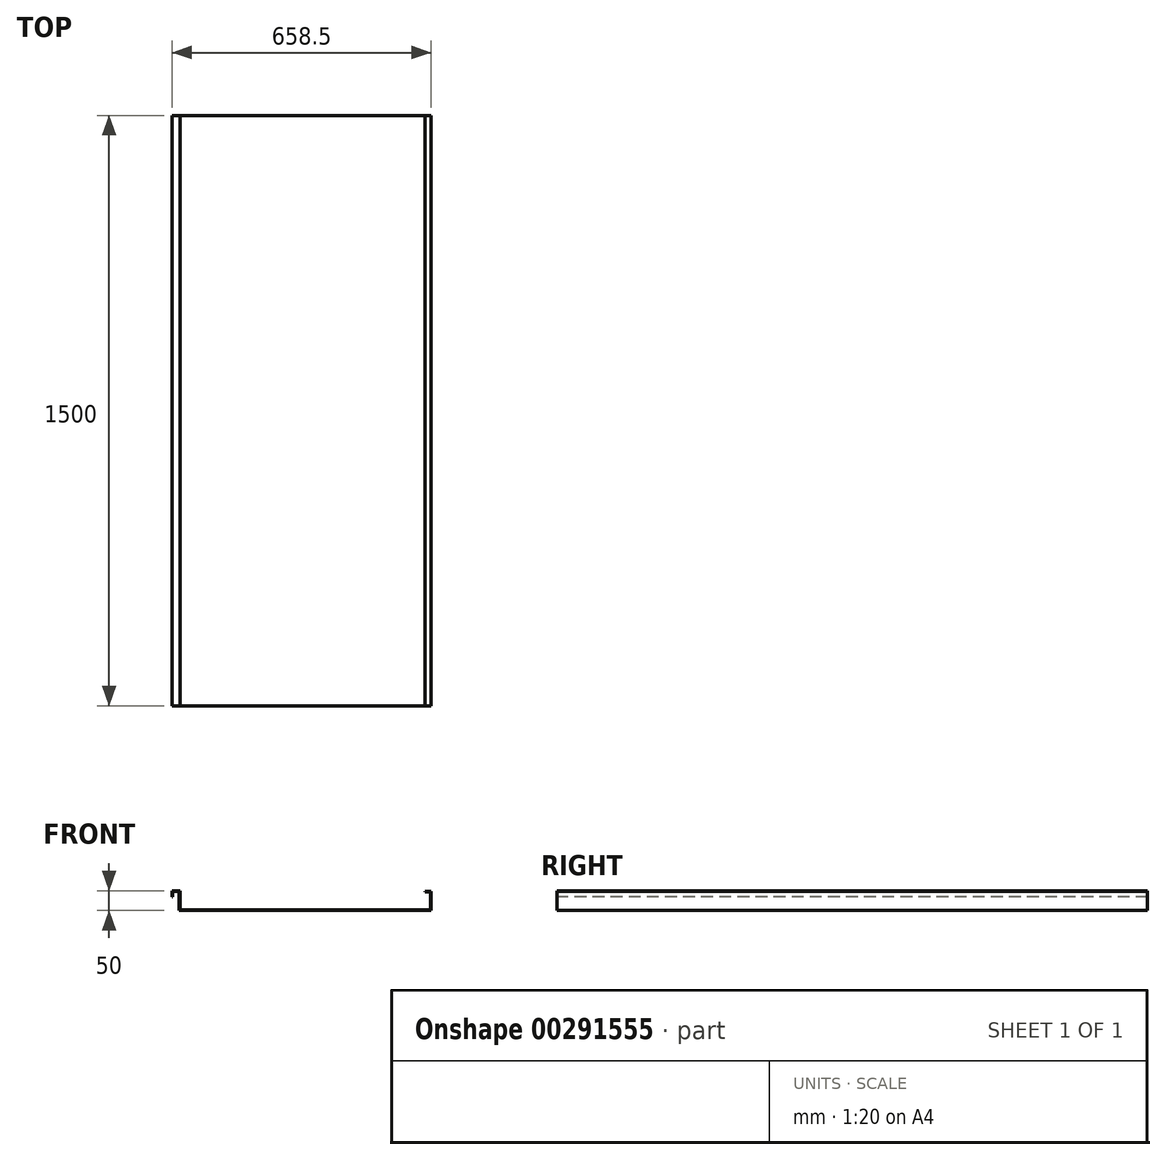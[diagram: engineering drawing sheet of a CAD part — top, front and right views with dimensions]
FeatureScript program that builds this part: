
annotation { "Feature Type Name" : "Feature", "Feature Type Description" : "" }
export const myFeature = defineFeature(function(context is Context, id is Id, definition is map)
    precondition{}
    {
        {
            var Q0;
            Q0=qCreatedBy(makeId("Front.planeOp"),FACE);
            var sketch = newSketch(context, id + "F0", { "sketchPlane" : qUnion([Q0])});
            skLineSegment(sketch, "E0", {"start": v(9.56, 16.63) * mm, "end": v(649.56, 16.63) * mm});
            skLineSegment(sketch, "E1", {"start": v(649.56, 16.63) * mm, "end": v(649.56, 65.13) * mm});
            skLineSegment(sketch, "E2", {"start": v(649.56, 65.13) * mm, "end": v(633.56, 65.13) * mm});
            skLineSegment(sketch, "E3", {"start": v(633.56, 65.13) * mm, "end": v(633.56, 63.63) * mm});
            skLineSegment(sketch, "E4", {"start": v(633.56, 63.63) * mm, "end": v(648.06, 63.63) * mm});
            skLineSegment(sketch, "E5", {"start": v(9.56, 16.63) * mm, "end": v(9.56, 65.13) * mm});
            skLineSegment(sketch, "E6", {"start": v(648.06, 63.63) * mm, "end": v(648.06, 18.13) * mm});
            skLineSegment(sketch, "E7", {"start": v(648.06, 18.13) * mm, "end": v(11.06, 18.13) * mm});
            skLineSegment(sketch, "E8", {"start": v(11.06, 18.13) * mm, "end": v(11.06, 66.63) * mm});
            skLineSegment(sketch, "E9", {"start": v(11.06, 66.63) * mm, "end": v(-8.94, 66.63) * mm});
            skLineSegment(sketch, "E10", {"start": v(-8.94, 66.63) * mm, "end": v(-8.94, 51.63) * mm});
            skLineSegment(sketch, "E11", {"start": v(-8.94, 51.63) * mm, "end": v(-7.44, 51.63) * mm});
            skLineSegment(sketch, "E12", {"start": v(-7.44, 51.63) * mm, "end": v(-7.44, 65.13) * mm});
            skLineSegment(sketch, "E13", {"start": v(-7.44, 65.13) * mm, "end": v(9.56, 65.13) * mm});
            skSolve(sketch);
        }
        {
            var Q0;
            Q0=makeQuery(id+"F0.imprint","IMPRINT",FACE,{"disambiguationData":[TD([[makeQuery(id+"F0.imprint","IMPRINT",EDGE,{"derivedFrom":sQuery(id+"F0.wireOp",EDGE,"E0")}),1.0]])]});
            extrude(context, id + "F1", {"entities" : qUnion([Q0]), "oppositeDirection" : true, "depth" : 1500 * mm});
        }
    });
